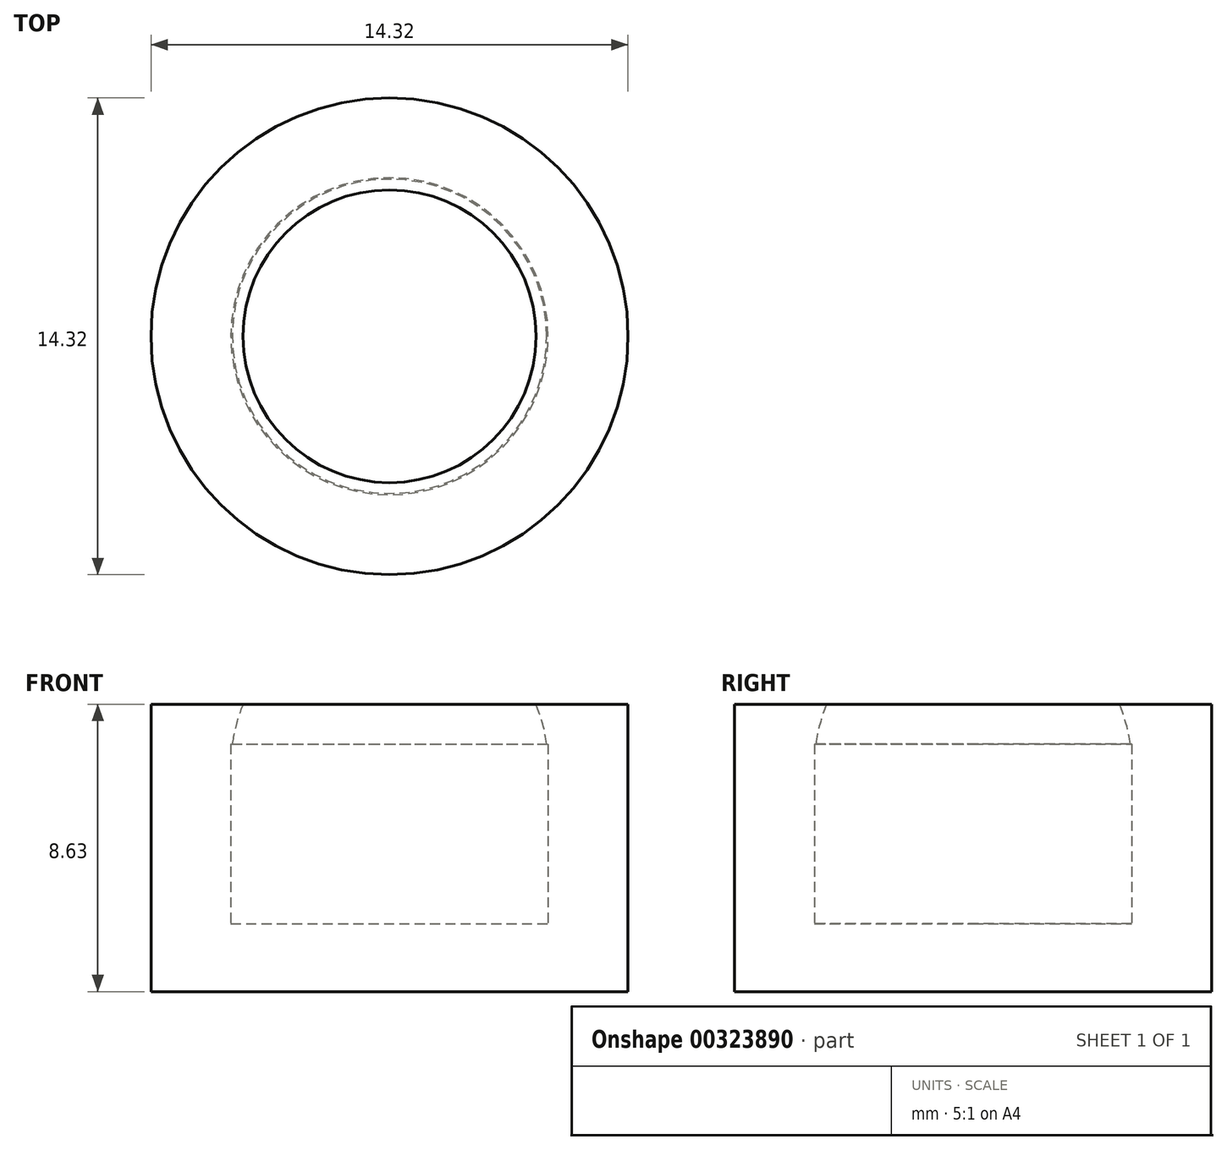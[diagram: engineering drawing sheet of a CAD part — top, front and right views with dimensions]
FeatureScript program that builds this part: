
annotation { "Feature Type Name" : "Feature", "Feature Type Description" : "" }
export const myFeature = defineFeature(function(context is Context, id is Id, definition is map)
    precondition{}
    {
        {
            var Q0;
            Q0=qCreatedBy(makeId("Front.planeOp"),FACE);
            var sketch = newSketch(context, id + "F0", { "sketchPlane" : qUnion([Q0])});
            skCircle(sketch, "E0", {"center": v(0, 0) * mm, "radius": 4.76 * mm, "construction": true});
            skLineSegment(sketch, "E1", {"start": v(-4.76, 1.83) * mm, "end": v(-7.16, 1.83) * mm});
            skLineSegment(sketch, "E2", {"start": v(-7.16, 1.83) * mm, "end": v(-7.16, -6.8) * mm});
            skLineSegment(sketch, "E3", {"start": v(-7.16, -6.8) * mm, "end": v(0, -6.8) * mm});
            skLineSegment(sketch, "E4", {"start": v(0, -6.8) * mm, "end": v(0, -4.76) * mm});
            skLineSegment(sketch, "E5", {"start": v(0, -4.76) * mm, "end": v(-4.76, -4.76) * mm});
            skLineSegment(sketch, "E6", {"start": v(-4.76, -4.76) * mm, "end": v(-4.76, 1.83) * mm});
            skLineSegment(sketch, "E7", {"start": v(0, 0) * mm, "end": v(0, 50.35) * mm, "construction": true});
            skArc(sketch, "E8", {"start": v(-4.4, 1.83) * mm, "mid": v(-4.6, 1.24) * mm, "end": v(-4.72, 0.63) * mm});
            skLineSegment(sketch, "E9", {"start": v(-4.72, 0.63) * mm, "end": v(-4.76, 0.63) * mm});
            skLineSegment(sketch, "E10", {"start": v(-4.76, 1.83) * mm, "end": v(-4.4, 1.83) * mm});
            skSolve(sketch);
        }
        {
            var Q0;
            Q0=makeQuery(id+"F0.imprint","IMPRINT",FACE,{"disambiguationData":[TD([[makeQuery(id+"F0.imprint","IMPRINT",EDGE,{"derivedFrom":sQuery(id+"F0.wireOp",EDGE,"E1")}),1.0]])]});
            var Q1;
            Q1=makeQuery(id+"F0.imprint","IMPRINT",FACE,{"disambiguationData":[TD([[makeQuery(id+"F0.imprint","IMPRINT",EDGE,{"derivedFrom":sQuery(id+"F0.wireOp",EDGE,"E8")}),-1.0]])]});
            var Q2;
            Q2=sQuery(id+"F0.wireOp",EDGE,"E4");
            revolve(context, id + "F1", {"entities" : qUnion([Q0, Q1]), "axis" : qUnion([Q2]), "revolveType" : RevolveType.FULL});
        }
    });
